# Revit family: Värmelampa Classic 1250
name_source: partatom
category: Lighting Fixtures
units: mm (PartAtom-declared; Revit-internal decimal feet)

## family parameters
Always vertical = Yes
Cut with Voids When Loaded = No
Host = Ceiling
Light Source = No
OmniClass Number = 23.80.70.11
OmniClass Title = Luminaries for Internal Lighting
Part Type = Normal
Room Calculation Point = No
Round Connector Dimension = Use Diameter
Shared = No

## types (6) — shared parameters
Lamp Hanger Material = AMA - Glossy Black Dark
zero-valued in all types: Default Elevation

## per-type parameters (varying)
| type | Artikelnummer | Lamp Type |
| 1250-S | 1250-S | Värmelampa Classic M 1250 : 1224-HSS |
| 1250-M | 1250-M | Värmelampa Classic M 1250 : 1224-HSM |
| 1250-A | 1250-A | Värmelampa Classic M 1250 : 1224-HSA |
| 1250-K | 1250-K | Värmelampa Classic M 1250 : 1224-HSK |
| 1250-SL | 1250-SL | Värmelampa Classic M 1250 : 1224-HSSL |
| 1250-C | 1250-M | Värmelampa Classic M 1250 : 1250-C |

## geometry (parser evidence)
native form markers: Sweep x5
no freeform markers — native parametric forms only
